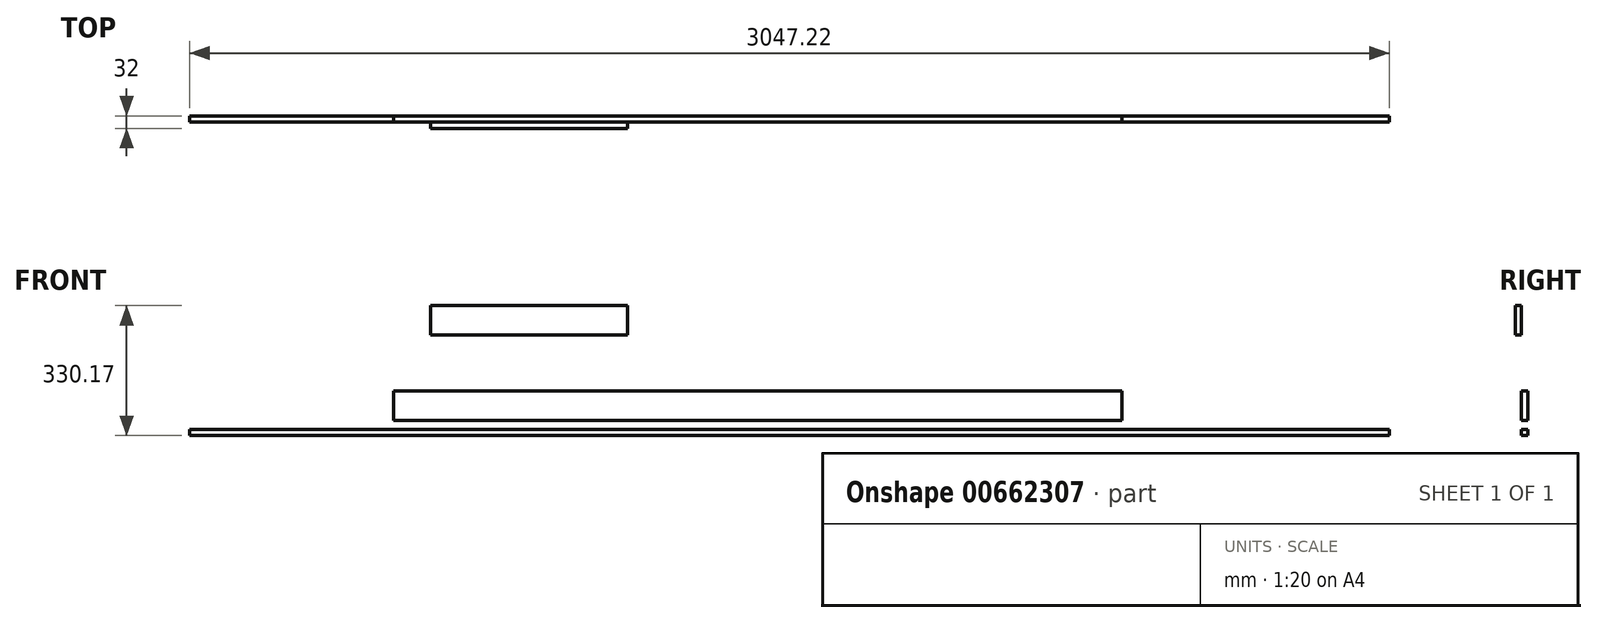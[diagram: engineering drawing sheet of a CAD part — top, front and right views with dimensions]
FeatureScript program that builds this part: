
annotation { "Feature Type Name" : "Feature", "Feature Type Description" : "" }
export const myFeature = defineFeature(function(context is Context, id is Id, definition is map)
    precondition{}
    {
        {
            var Q0;
            Q0=qCreatedBy(makeId("Front.planeOp"),FACE);
            var sketch = newSketch(context, id + "F0", { "sketchPlane" : qUnion([Q0])});
            skLineSegment(sketch, "E0.bottom", {"start": v(-1523.31, 45.92) * mm, "end": v(1523.91, 45.92) * mm});
            skLineSegment(sketch, "E0.top", {"start": v(-1523.31, -29.08) * mm, "end": v(1523.91, -29.08) * mm});
            skLineSegment(sketch, "E0.left", {"start": v(-1523.31, 45.92) * mm, "end": v(-1523.31, -29.08) * mm});
            skLineSegment(sketch, "E0.right", {"start": v(1523.91, 45.92) * mm, "end": v(1523.91, -29.08) * mm});
            skSolve(sketch);
        }
        {
            var Q0;
            Q0=sQuery(id+"F0.wireOp",EDGE,"E0.top");
            extrude(context, id + "F1", {"bodyType" : ToolBodyType.SURFACE, "surfaceEntities" : qUnion([Q0]), "depth" : 16 * mm, "offsetDistance" : 25 * mm});
        }
        {
            var Q0;
            Q0=qCreatedBy(makeId("Front.planeOp"),FACE);
            var sketch = newSketch(context, id + "F2", { "sketchPlane" : qUnion([Q0])});
            skLineSegment(sketch, "E1.right", {"start": v(1309.13, 310.9) * mm, "end": v(1309.13, 299.85) * mm});
            skLineSegment(sketch, "E2.bottom", {"start": v(-959.5, 362.2) * mm, "end": v(2755.5, 362.2) * mm});
            skLineSegment(sketch, "E2.top", {"start": v(-959.5, 287.2) * mm, "end": v(2755.5, 287.2) * mm});
            skLineSegment(sketch, "E2.left", {"start": v(-959.5, 362.2) * mm, "end": v(-959.5, 287.2) * mm});
            skLineSegment(sketch, "E2.right", {"start": v(2755.5, 362.2) * mm, "end": v(2755.5, 287.2) * mm});
            skSolve(sketch);
        }
        {
            var Q0;
            Q0=makeQuery(id+"F1.opExtrude","SWEPT_FACE",FACE,{"disambiguationData":[OSD([sQuery(id+"F0.wireOp",EDGE,"E0.top")])]});
            extrude(context, id + "F3", {"entities" : qUnion([Q0]), "depth" : 16 * mm, "offsetDistance" : 25 * mm});
        }
        {
            var Q0;
            Q0=sQuery(id+"F2.wireOp",EDGE,"E2.bottom");
            extrude(context, id + "F4", {"bodyType" : ToolBodyType.SURFACE, "surfaceEntities" : qUnion([Q0]), "depth" : 16 * mm, "offsetDistance" : 25 * mm});
        }
        {
            var Q0;
            Q0=makeQuery(id+"F4.opExtrude","SWEPT_BODY",BODY,{"disambiguationData":[OSD([sQuery(id+"F2.wireOp",EDGE,"E2.bottom")])]});
            var Q1;
            Q1=makeQuery(id+"F1.opExtrude","SWEPT_BODY",BODY,{"disambiguationData":[OSD([sQuery(id+"F0.wireOp",EDGE,"E0.top")])]});
            deleteBodies(context, id + "F5", {"entities" : qUnion([Q0, Q1])});
        }
        {
            var Q0;
            Q0=qCreatedBy(makeId("Front.planeOp"),FACE);
            var sketch = newSketch(context, id + "F6", { "sketchPlane" : qUnion([Q0])});
            skLineSegment(sketch, "E3.bottom", {"start": v(-1004.9, 68.58) * mm, "end": v(845.1, 68.58) * mm});
            skLineSegment(sketch, "E3.top", {"start": v(-1004.9, -6.42) * mm, "end": v(845.1, -6.42) * mm});
            skLineSegment(sketch, "E3.left", {"start": v(-1004.9, 68.58) * mm, "end": v(-1004.9, -6.42) * mm});
            skLineSegment(sketch, "E3.right", {"start": v(845.1, 68.58) * mm, "end": v(845.1, -6.42) * mm});
            skSolve(sketch);
        }
        {
            var Q0;
            Q0=makeQuery(id+"F6.imprint","IMPRINT",FACE,{"disambiguationData":[TD([[makeQuery(id+"F6.imprint","IMPRINT",EDGE,{"derivedFrom":sQuery(id+"F6.wireOp",EDGE,"E3.bottom")}),-1.0]])]});
            extrude(context, id + "F7", {"entities" : qUnion([Q0]), "depth" : 16 * mm, "offsetDistance" : 25 * mm});
        }
        {
            var Q0;
            Q0=makeQuery(id+"F7.opExtrude","CAP_FACE",FACE,{"disambiguationData":[OSD([sQuery(id+"F6.wireOp",EDGE,"E3.bottom"),sQuery(id+"F6.wireOp",EDGE,"E3.top"),sQuery(id+"F6.wireOp",EDGE,"E3.left"),sQuery(id+"F6.wireOp",EDGE,"E3.right")])],"isStart":false});
            var sketch = newSketch(context, id + "F8", { "sketchPlane" : qUnion([Q0])});
            skLineSegment(sketch, "E4.bottom", {"start": v(-911.01, 285.09) * mm, "end": v(-411.01, 285.09) * mm});
            skLineSegment(sketch, "E4.top", {"start": v(-911.01, 210.09) * mm, "end": v(-411.01, 210.09) * mm});
            skLineSegment(sketch, "E4.left", {"start": v(-911.01, 285.09) * mm, "end": v(-911.01, 210.09) * mm});
            skLineSegment(sketch, "E4.right", {"start": v(-411.01, 285.09) * mm, "end": v(-411.01, 210.09) * mm});
            skSolve(sketch);
        }
        {
            var Q0;
            Q0=makeQuery(id+"F8.imprint","IMPRINT",FACE,{"disambiguationData":[TD([[makeQuery(id+"F8.imprint","IMPRINT",EDGE,{"derivedFrom":sQuery(id+"F8.wireOp",EDGE,"E4.bottom")}),-1.0]])]});
            extrude(context, id + "F9", {"entities" : qUnion([Q0]), "depth" : 16 * mm, "offsetDistance" : 25 * mm});
        }
    });
